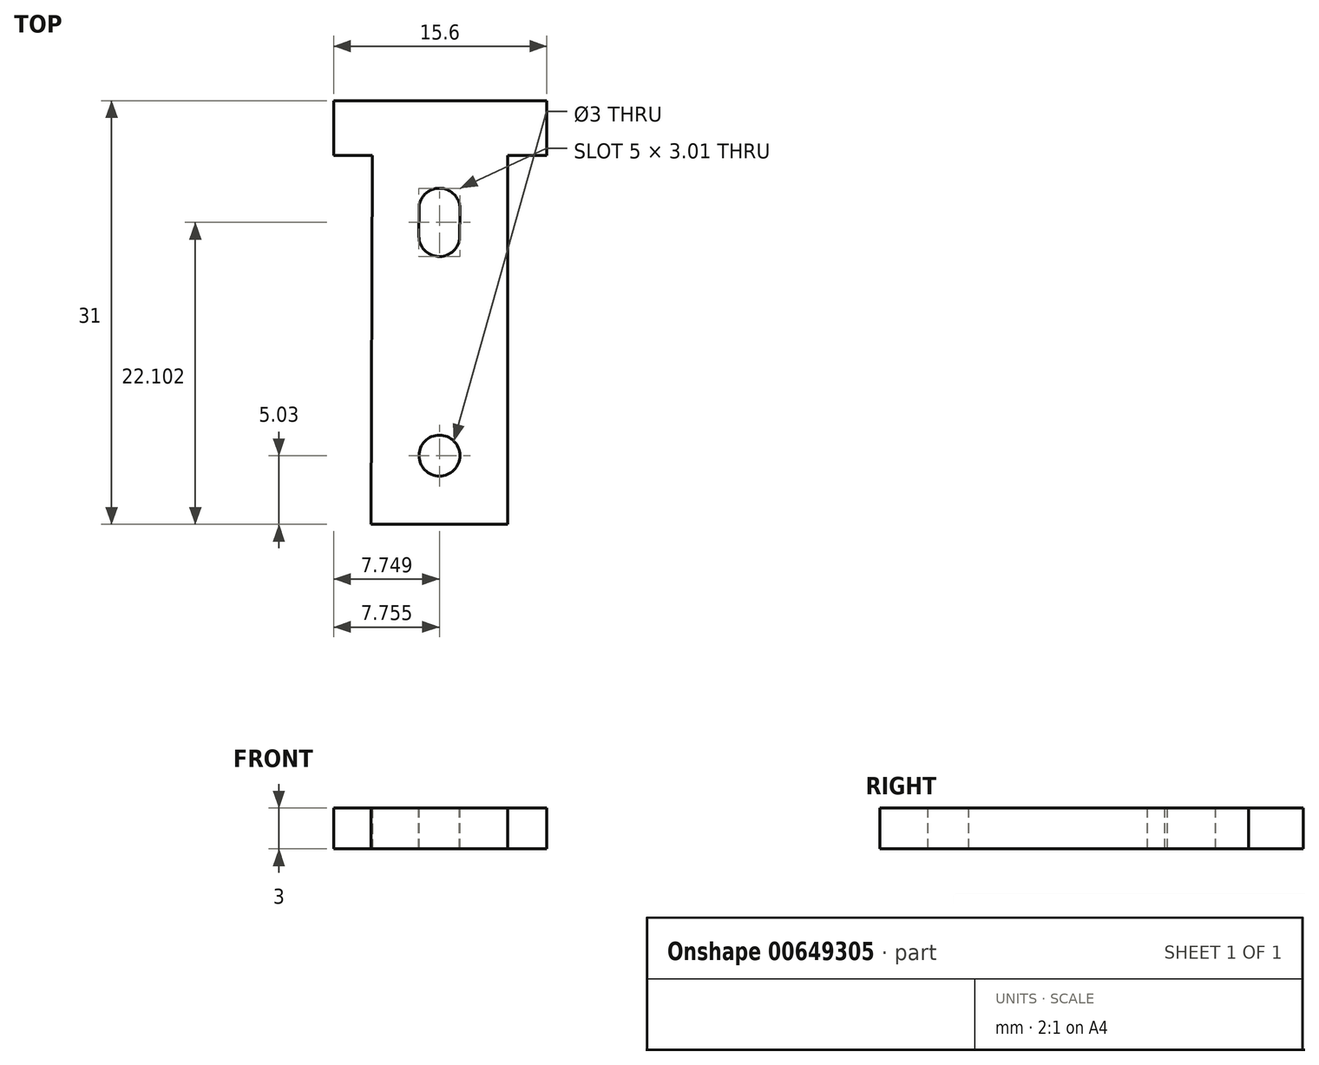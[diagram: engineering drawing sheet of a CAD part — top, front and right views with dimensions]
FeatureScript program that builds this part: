
annotation { "Feature Type Name" : "Feature", "Feature Type Description" : "" }
export const myFeature = defineFeature(function(context is Context, id is Id, definition is map)
    precondition{}
    {
        {
            var Q0;
            Q0=qCreatedBy(makeId("Top.planeOp"),FACE);
            var sketch = newSketch(context, id + "F0", { "sketchPlane" : qUnion([Q0])});
            skLineSegment(sketch, "E0", {"start": v(-3.2, -19.6) * mm, "end": v(-3.2, 7.4) * mm});
            skLineSegment(sketch, "E1", {"start": v(-3.2, 7.4) * mm, "end": v(-0.35, 7.4) * mm});
            skLineSegment(sketch, "E2", {"start": v(-0.35, 7.4) * mm, "end": v(-0.35, 11.4) * mm});
            skLineSegment(sketch, "E3", {"start": v(-0.35, 11.4) * mm, "end": v(-15.95, 11.4) * mm});
            skLineSegment(sketch, "E4", {"start": v(-15.95, 11.4) * mm, "end": v(-15.95, 7.4) * mm});
            skLineSegment(sketch, "E5", {"start": v(-13.2, -19.6) * mm, "end": v(-3.2, -19.6) * mm});
            skLineSegment(sketch, "E6", {"start": v(-15.95, 7.4) * mm, "end": v(-13.1, 7.4) * mm});
            skLineSegment(sketch, "E7", {"start": v(-13.1, 7.4) * mm, "end": v(-13.2, -19.6) * mm});
            skSolve(sketch);
        }
        {
            var Q0;
            Q0=makeQuery(id+"F0.imprint","IMPRINT",FACE,{"disambiguationData":[TD([[makeQuery(id+"F0.imprint","IMPRINT",EDGE,{"derivedFrom":sQuery(id+"F0.wireOp",EDGE,"E0")}),1.0]])]});
            extrude(context, id + "F1", {"entities" : qUnion([Q0]), "depth" : 3 * mm, "offsetDistance" : 25 * mm});
        }
        {
            var Q0;
            Q0=makeQuery(id+"F1.opExtrude","CAP_FACE",FACE,{"disambiguationData":[OSD([sQuery(id+"F0.wireOp",EDGE,"E0"),sQuery(id+"F0.wireOp",EDGE,"E1"),sQuery(id+"F0.wireOp",EDGE,"E2"),sQuery(id+"F0.wireOp",EDGE,"E3"),sQuery(id+"F0.wireOp",EDGE,"E4"),sQuery(id+"F0.wireOp",EDGE,"E5"),sQuery(id+"F0.wireOp",EDGE,"E6"),sQuery(id+"F0.wireOp",EDGE,"E7")])],"isStart":false});
            var sketch = newSketch(context, id + "F2", { "sketchPlane" : qUnion([Q0])});
            skCircle(sketch, "E8", {"center": v(-8.2, -14.57) * mm, "radius": 1.5 * mm});
            skLineSegment(sketch, "E9", {"start": v(-8.2, -19.6) * mm, "end": v(-8.2, 11.4) * mm, "construction": true});
            skArc(sketch, "E10", {"start": v(-9.7, 1.55) * mm, "mid": v(-8.35, 0) * mm, "end": v(-6.73, 1.27) * mm});
            skPoint(sketch, "E10.first.point", {"position": v(-8.2, 3) * mm});
            skPoint(sketch, "E10.second.point", {"position": v(-8.2, 0) * mm});
            skPoint(sketch, "E10.second.point.positionSnap0", {"position": v(-8.2, -4.1) * mm});
            skPoint(sketch, "E10.third.point", {"position": v(-9.7, 1.47) * mm});
            skArc(sketch, "E11", {"start": v(-6.7, 3.47) * mm, "mid": v(-8.18, 5) * mm, "end": v(-9.7, 3.5) * mm});
            skPoint(sketch, "E12", {"position": v(-8.2, 2.18) * mm});
            skLineSegment(sketch, "E13", {"start": v(-9.7, 3.5) * mm, "end": v(-9.7, 1.47) * mm});
            skLineSegment(sketch, "E14", {"start": v(-6.7, 3.47) * mm, "end": v(-6.73, 1.27) * mm});
            skSolve(sketch);
        }
        {
            var Q0;
            {var subQ4=sQuery(id+"F2.wireOp",EDGE,"E11");Q0=makeQuery(id+"F2.imprint","IMPRINT",FACE,{"disambiguationData":[TD([[makeQuery(id+"F2.imprint","IMPRINT",EDGE,{"derivedFrom":subQ4}),1.0]])]});}
            var Q1;
            Q1=makeQuery(id+"F2.imprint","IMPRINT",FACE,{"disambiguationData":[TD([[makeQuery(id+"F2.imprint","IMPRINT",EDGE,{"derivedFrom":sQuery(id+"F2.wireOp",EDGE,"E8")}),1.0]])]});
            extrude(context, id + "F3", {"entities" : qUnion([Q0, Q1]), "operationType" : NewBodyOperationType.REMOVE, "endBound" : BoundingType.THROUGH_ALL, "oppositeDirection" : true, "depth" : 25 * mm, "offsetDistance" : 25 * mm});
        }
    });
